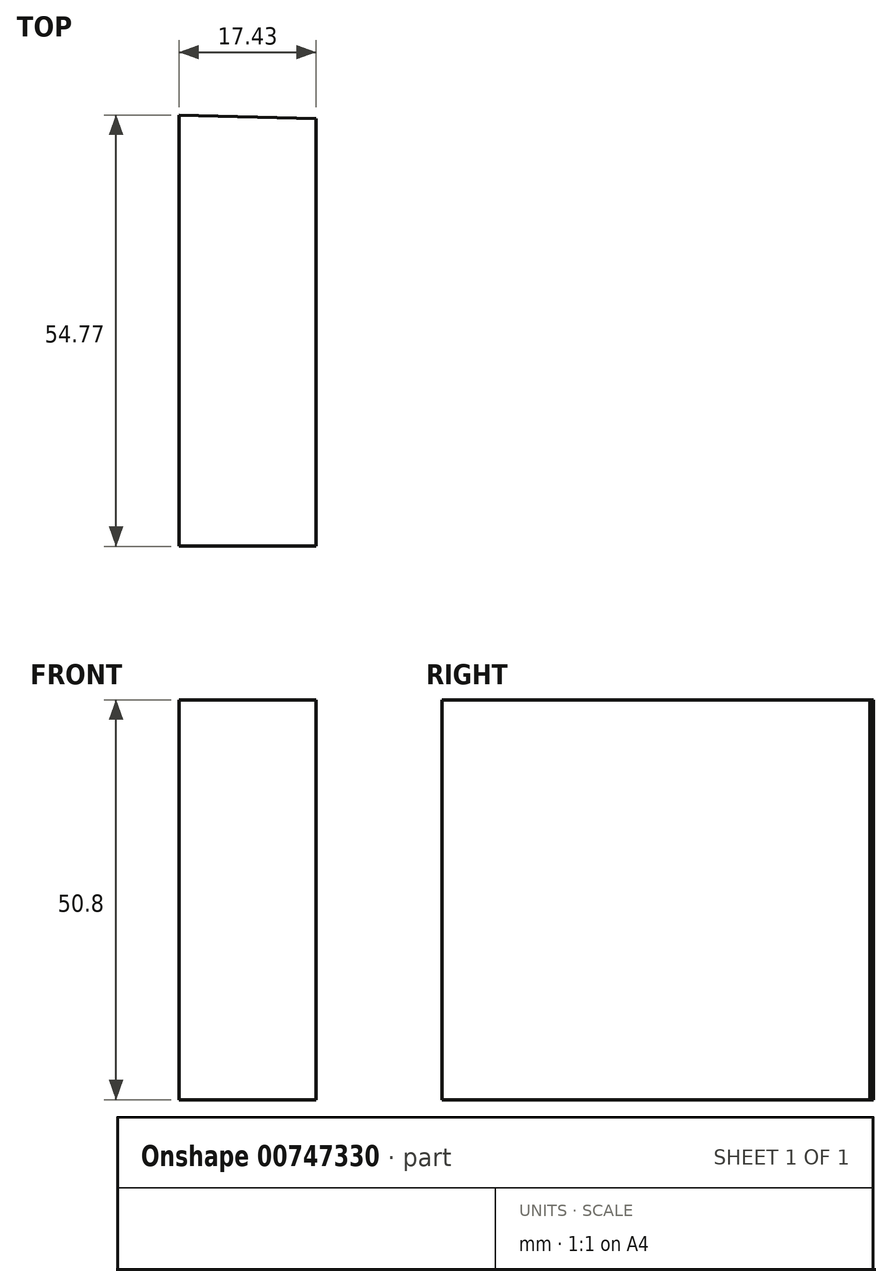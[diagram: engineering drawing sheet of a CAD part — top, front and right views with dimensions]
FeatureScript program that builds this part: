
annotation { "Feature Type Name" : "Feature", "Feature Type Description" : "" }
export const myFeature = defineFeature(function(context is Context, id is Id, definition is map)
    precondition{}
    {
        {
            var Q0;
            Q0=qCreatedBy(makeId("Top.planeOp"),FACE);
            var sketch = newSketch(context, id + "F0", { "sketchPlane" : qUnion([Q0])});
            skLineSegment(sketch, "E0", {"start": v(-17.43, 27.6) * mm, "end": v(-17.43, -27.18) * mm});
            skLineSegment(sketch, "E1", {"start": v(-17.43, -27.18) * mm, "end": v(0, -27.18) * mm});
            skLineSegment(sketch, "E2", {"start": v(0, -27.18) * mm, "end": v(0, 27.18) * mm});
            skLineSegment(sketch, "E3", {"start": v(0, 27.18) * mm, "end": v(-17.43, 27.6) * mm});
            skSolve(sketch);
        }
        {
            var Q0;
            Q0=sQuery(id+"F0.wireOp",EDGE,"E0");
            var Q1;
            Q1=sQuery(id+"F0.wireOp",EDGE,"E2");
            var Q2;
            Q2=sQuery(id+"F0.wireOp",EDGE,"E1");
            var Q3;
            Q3=sQuery(id+"F0.wireOp",EDGE,"E3");
            extrude(context, id + "F1", {"bodyType" : ToolBodyType.SURFACE, "surfaceEntities" : qUnion([Q0, Q1, Q2, Q3]), "oppositeDirection" : true, "depth" : 50.8 * mm, "offsetDistance" : 25.4 * mm});
        }
    });
